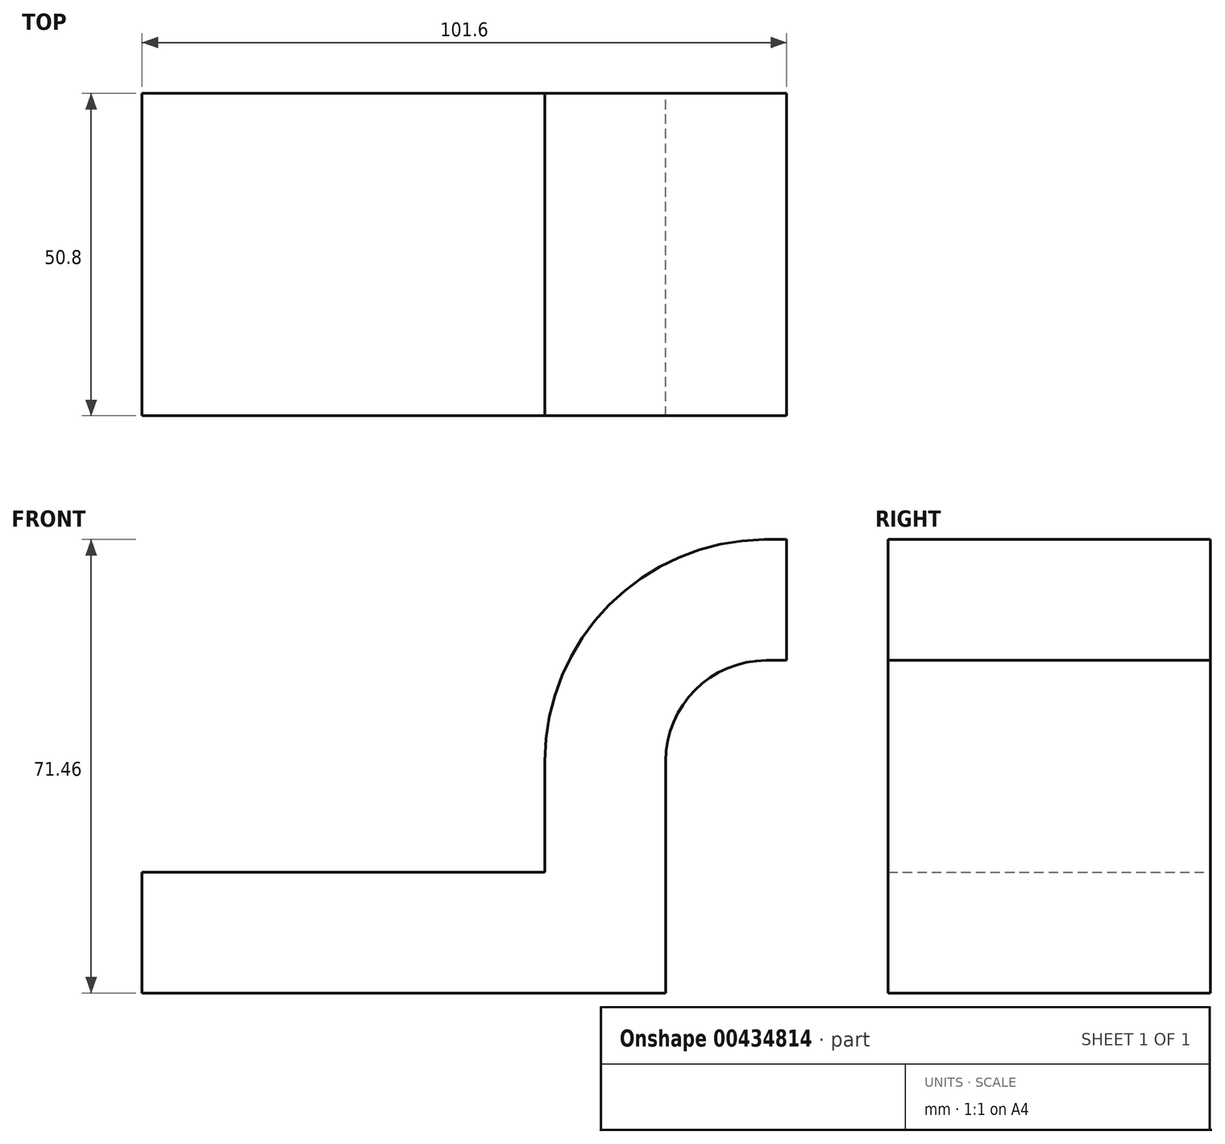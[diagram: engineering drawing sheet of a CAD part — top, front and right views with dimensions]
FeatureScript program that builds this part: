
annotation { "Feature Type Name" : "Feature", "Feature Type Description" : "" }
export const myFeature = defineFeature(function(context is Context, id is Id, definition is map)
    precondition{}
    {
        {
            var Q0;
            Q0=qCreatedBy(makeId("Front.planeOp"),FACE);
            var sketch = newSketch(context, id + "F0", { "sketchPlane" : qUnion([Q0])});
            skLineSegment(sketch, "E0.bottom", {"start": v(-41.28, 9.52) * mm, "end": v(41.27, 9.53) * mm});
            skLineSegment(sketch, "E0.top", {"start": v(-41.28, -9.53) * mm, "end": v(41.28, -9.53) * mm});
            skLineSegment(sketch, "E0.left", {"start": v(-41.28, 9.52) * mm, "end": v(-41.27, -9.53) * mm});
            skLineSegment(sketch, "E0.right", {"start": v(41.28, 9.53) * mm, "end": v(41.28, -9.52) * mm});
            skPoint(sketch, "E0.middle", {"position": v(0, 0) * mm});
            skLineSegment(sketch, "E1.bottom", {"start": v(111.12, 38.1) * mm, "end": v(60.32, 38.1) * mm});
            skLineSegment(sketch, "E1.top", {"start": v(111.12, 66.68) * mm, "end": v(60.32, 66.68) * mm});
            skLineSegment(sketch, "E1.left", {"start": v(111.12, 38.1) * mm, "end": v(111.12, 66.68) * mm});
            skLineSegment(sketch, "E1.right", {"start": v(60.32, 38.1) * mm, "end": v(60.32, 66.68) * mm});
            skPoint(sketch, "E1.middle", {"position": v(85.72, 52.39) * mm});
            skLineSegment(sketch, "E2", {"start": v(41.27, 9.53) * mm, "end": v(41.27, 27) * mm});
            skArc(sketch, "E3", {"start": v(41.27, 27) * mm, "mid": v(45.92, 38.23) * mm, "end": v(57.15, 42.88) * mm});
            skLineSegment(sketch, "E4", {"start": v(57.15, 42.88) * mm, "end": v(85.72, 42.88) * mm});
            skLineSegment(sketch, "E5.0", {"start": v(57.15, 61.93) * mm, "end": v(85.72, 61.93) * mm});
            skArc(sketch, "E5.1", {"start": v(22.23, 27) * mm, "mid": v(32.45, 51.7) * mm, "end": v(57.15, 61.93) * mm});
            skLineSegment(sketch, "E5.2", {"start": v(22.22, 9.53) * mm, "end": v(22.22, 27) * mm});
            skLineSegment(sketch, "E6", {"start": v(85.72, 42.88) * mm, "end": v(85.72, 66.68) * mm});
            skFitSpline(sketch, "E7", {"points": [v(-41.28, 9.52) * mm, v(57.15, 61.93) * mm], "startDerivative": vector(1.53, 93.15) * mm, "endDerivative": vector(114.57, 0.35) * mm});
            skSolve(sketch);
        }
        {
            var Q0;
            Q0=makeQuery(id+"F0.imprint","IMPRINT",FACE,{"disambiguationData":[TD([[makeQuery(id+"F0.imprint","IMPRINT",EDGE,{"derivedFrom":sQuery(id+"F0.wireOp",EDGE,"E0.top")}),1.0]])]});
            var Q1;
            {var subQ1=sQuery(id+"F0.wireOp",EDGE,"E2");Q1=makeQuery(id+"F0.imprint","IMPRINT",FACE,{"disambiguationData":[TD([[makeQuery(id+"F0.imprint","IMPRINT",EDGE,{"derivedFrom":subQ1}),1.0]])]});}
            extrude(context, id + "F1", {"entities" : qUnion([Q0, Q1]), "endBound" : BoundingType.SYMMETRIC, "depth" : 50.8 * mm});
        }
        {
            var Q0;
            {var subQ4=sQuery(id+"F0.wireOp",EDGE,"E5.1");Q0=makeQuery(id+"F0.imprint","IMPRINT",FACE,{"disambiguationData":[TD([[makeQuery(id+"F0.imprint","IMPRINT",EDGE,{"derivedFrom":subQ4}),1.0]])]});}
            extrude(context, id + "F2", {"entities" : qUnion([Q0]), "operationType" : NewBodyOperationType.ADD, "endBound" : BoundingType.SYMMETRIC, "depth" : 15.88 * mm});
        }
    });
